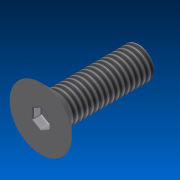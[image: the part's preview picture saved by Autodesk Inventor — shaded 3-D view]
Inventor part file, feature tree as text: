
AUTODESK INVENTOR PART (.ipt)
format: ipt  version: 2013 (Build 170138000, 138)  size: 166,912 bytes
history: native  units: mm
features: sketch x3, extrude x2, other x1, revolve x1, chamfer x1, fillet x1, thread x1
ambient origin geometry x1: Origin
feature tree (10):
  other  "ソリッド1"
  revolve  "回転1"
  extrude  "押し出し1"  TaperAngle=45.0deg  [1 undecoded]
  extrude  "押し出し2"  Depth=3.0mm
  chamfer  "面取り1"  Distance=1.5mm
  fillet  "フィレット1"  [1 undecoded]
  thread  "ねじ2"
  sketch  "スケッチ1"
  sketch  "スケッチ2"
  sketch  "スケッチ3"
note: 2 required parameter values undecoded (feature->parameter linkage not recoverable at this tier; creation-order binding heuristic only, values carry confidence <= 0.55)
